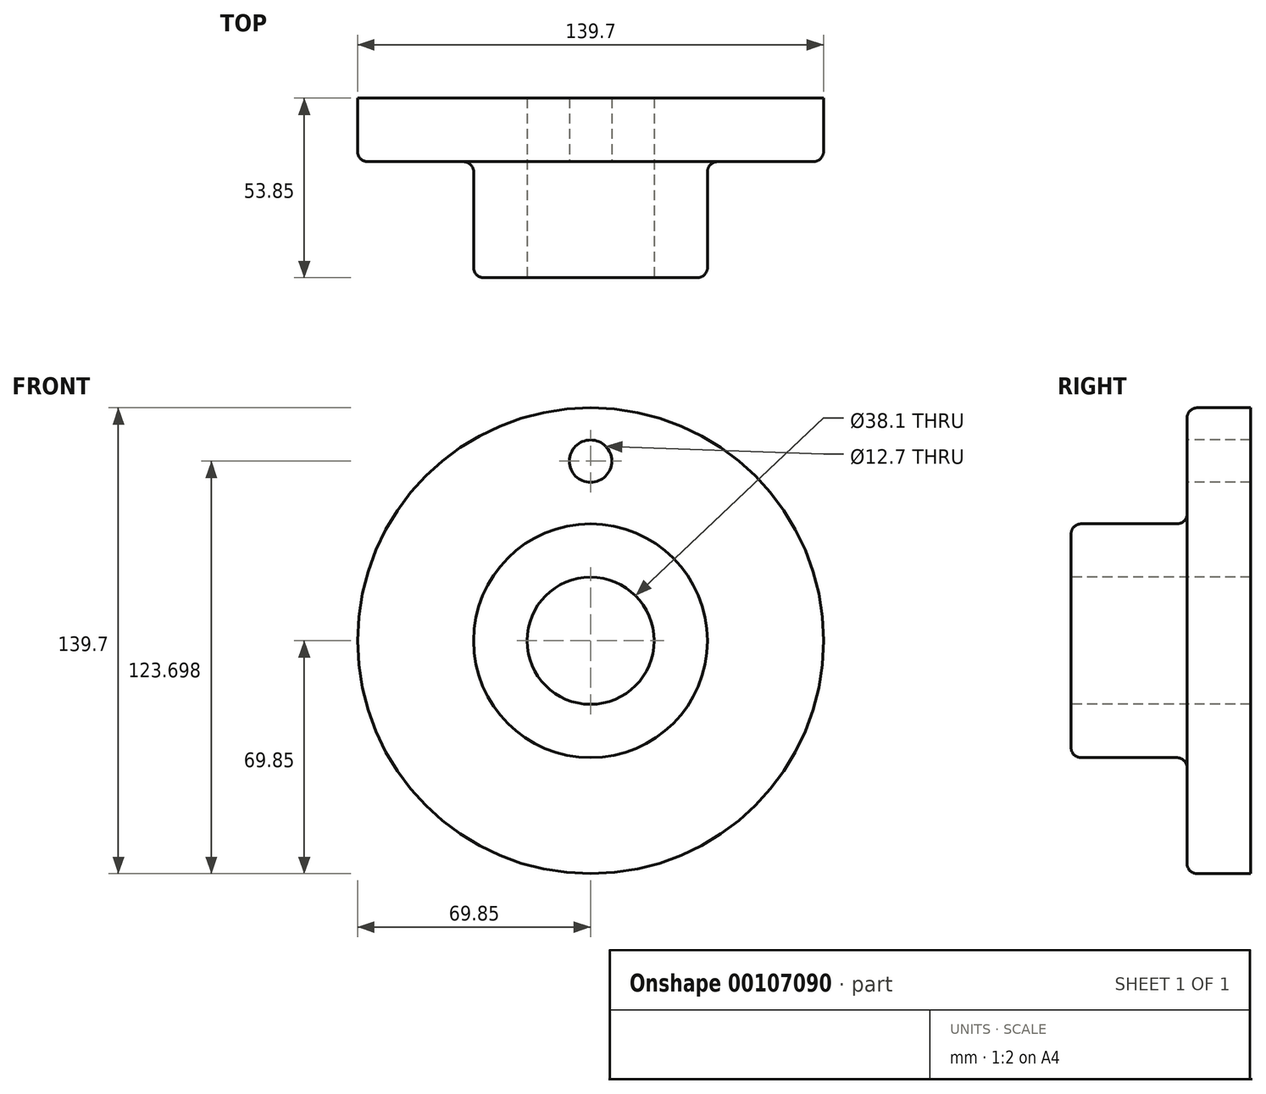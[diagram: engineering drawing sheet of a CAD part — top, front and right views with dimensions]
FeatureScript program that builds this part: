
annotation { "Feature Type Name" : "Feature", "Feature Type Description" : "" }
export const myFeature = defineFeature(function(context is Context, id is Id, definition is map)
    precondition{}
    {
        {
            var Q0;
            Q0=qCreatedBy(makeId("Right.planeOp"),FACE);
            var sketch = newSketch(context, id + "F0", { "sketchPlane" : qUnion([Q0])});
            skLineSegment(sketch, "E0", {"start": v(53.85, 19.05) * mm, "end": v(53.85, 69.85) * mm});
            skLineSegment(sketch, "E1", {"start": v(53.85, 69.85) * mm, "end": v(34.8, 69.85) * mm});
            skLineSegment(sketch, "E2", {"start": v(34.8, 69.85) * mm, "end": v(34.8, 35.05) * mm});
            skLineSegment(sketch, "E3", {"start": v(34.8, 35.05) * mm, "end": v(0, 35.05) * mm});
            skLineSegment(sketch, "E4", {"start": v(0, 35.05) * mm, "end": v(0, 19.05) * mm});
            skLineSegment(sketch, "E5", {"start": v(-8.72, 0) * mm, "end": v(76.6, 0) * mm, "construction": true});
            skLineSegment(sketch, "E6", {"start": v(0, 19.05) * mm, "end": v(53.85, 19.05) * mm});
            skPoint(sketch, "E7.start.orphan", {"position": v(0, 0) * mm});
            skPoint(sketch, "E8.orphan", {"position": v(53.85, 0) * mm});
            skSolve(sketch);
        }
        {
            var Q0;
            Q0=makeQuery(id+"F0.imprint","IMPRINT",FACE,{"disambiguationData":[TD([[makeQuery(id+"F0.imprint","IMPRINT",EDGE,{"derivedFrom":sQuery(id+"F0.wireOp",EDGE,"E0")}),1.0]])]});
            var Q1;
            Q1=sQuery(id+"F0.wireOp",EDGE,"E5");
            revolve(context, id + "F1", {"entities" : qUnion([Q0]), "axis" : qUnion([Q1]), "revolveType" : RevolveType.FULL});
        }
        {
            var Q0;
            Q0=makeQuery(id+"F1.opRevolve","SWEPT_EDGE",EDGE,{"disambiguationData":[OSD([sQuery(id+"F0.wireOp",EDGE,"E1"),sQuery(id+"F0.wireOp",EDGE,"E2")])]});
            var Q1;
            Q1=makeQuery(id+"F1.opRevolve","SWEPT_EDGE",EDGE,{"disambiguationData":[OSD([sQuery(id+"F0.wireOp",EDGE,"E2"),sQuery(id+"F0.wireOp",EDGE,"E3")])]});
            var Q2;
            Q2=makeQuery(id+"F1.opRevolve","SWEPT_EDGE",EDGE,{"disambiguationData":[OSD([sQuery(id+"F0.wireOp",EDGE,"E3"),sQuery(id+"F0.wireOp",EDGE,"E4")])]});
            fillet(context, id + "F2", {"entities" : qUnion([Q0, Q1, Q2]), "radius" : 3.05 * mm, "tangentPropagation" : true, "allowEdgeOverflow" : false});
        }
        {
            var Q0;
            Q0=makeQuery(id+"F1.opRevolve","SWEPT_FACE",FACE,{"disambiguationData":[OSD([sQuery(id+"F0.wireOp",EDGE,"E2")])]});
            var sketch = newSketch(context, id + "F3", { "sketchPlane" : qUnion([Q0])});
            skCircle(sketch, "E9", {"center": v(0, 53.85) * mm, "radius": 6.35 * mm});
            skCircle(sketch, "E10", {"center": v(0, 0) * mm, "radius": 53.85 * mm, "construction": true});
            skSolve(sketch);
        }
        {
            var Q0;
            Q0 = qSketchRegion(id + "F3", true);
            extrude(context, id + "F4", {"entities" : qUnion([Q0]), "operationType" : NewBodyOperationType.REMOVE, "endBound" : BoundingType.THROUGH_ALL, "oppositeDirection" : true, "depth" : 25.4 * mm});
        }
    });
